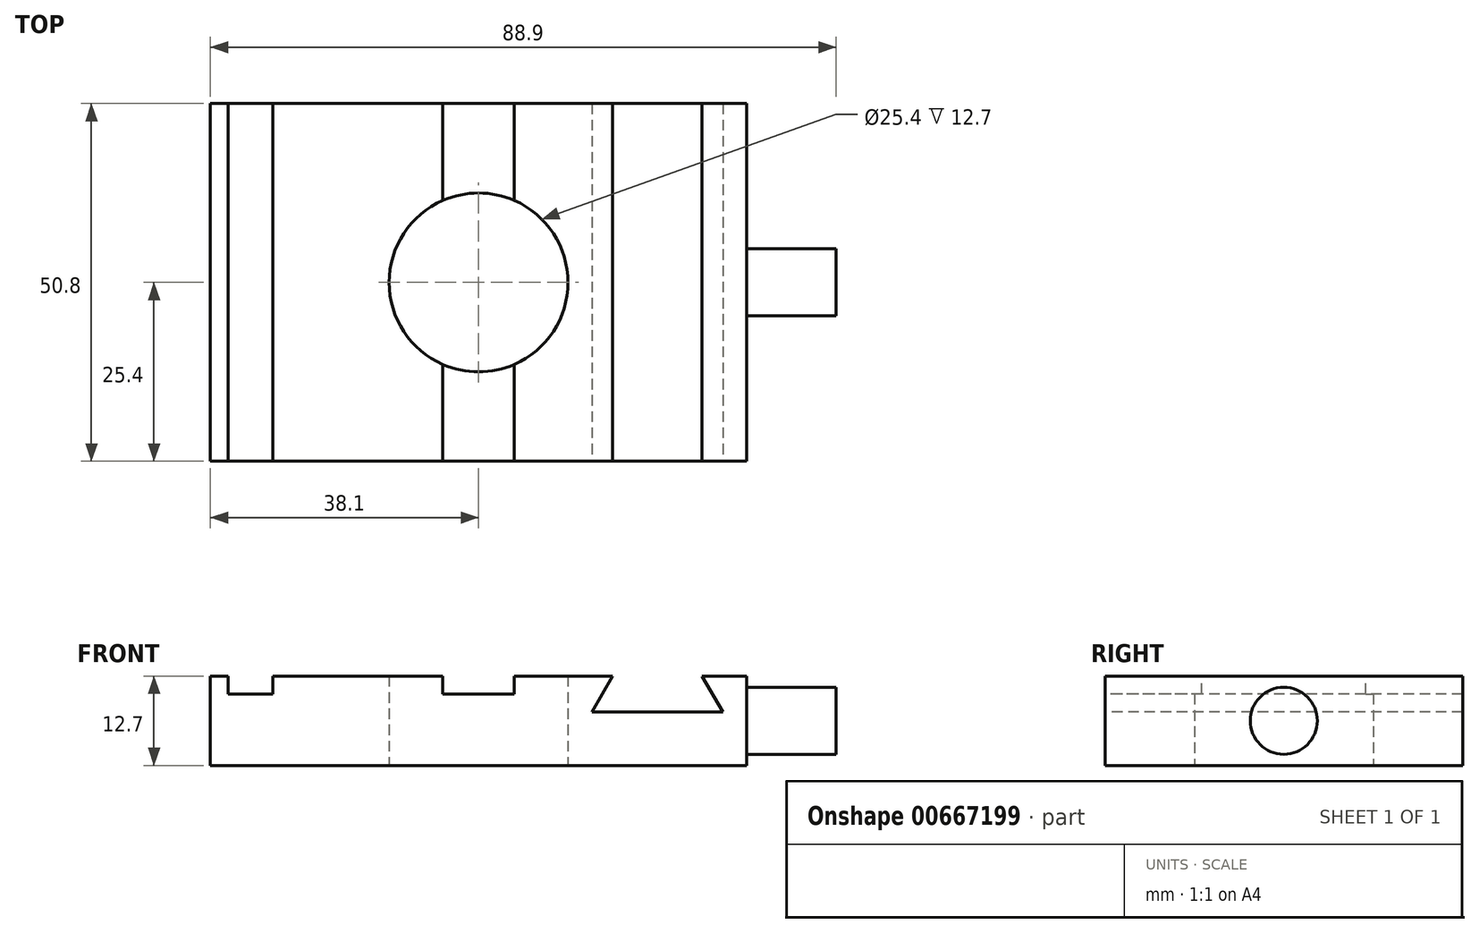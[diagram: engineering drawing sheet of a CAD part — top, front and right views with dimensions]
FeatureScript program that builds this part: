
annotation { "Feature Type Name" : "Feature", "Feature Type Description" : "" }
export const myFeature = defineFeature(function(context is Context, id is Id, definition is map)
    precondition{}
    {
        {
            var Q0;
            Q0=qCreatedBy(makeId("Top.planeOp"),FACE);
            var sketch = newSketch(context, id + "F0", { "sketchPlane" : qUnion([Q0])});
            skLineSegment(sketch, "E0.bottom", {"start": v(38.1, 25.4) * mm, "end": v(-38.1, 25.4) * mm});
            skLineSegment(sketch, "E0.top", {"start": v(38.1, -25.4) * mm, "end": v(-38.1, -25.4) * mm});
            skLineSegment(sketch, "E0.left", {"start": v(38.1, 25.4) * mm, "end": v(38.1, -25.4) * mm});
            skLineSegment(sketch, "E0.right", {"start": v(-38.1, 25.4) * mm, "end": v(-38.1, -25.4) * mm});
            skPoint(sketch, "E0.middle", {"position": v(0, 0) * mm});
            skCircle(sketch, "E1", {"center": v(0, 0) * mm, "radius": 12.7 * mm});
            skSolve(sketch);
        }
        {
            var Q0;
            Q0=makeQuery(id+"F0.imprint","IMPRINT",FACE,{"disambiguationData":[TD([[makeQuery(id+"F0.imprint","IMPRINT",EDGE,{"derivedFrom":sQuery(id+"F0.wireOp",EDGE,"E0.bottom")}),1.0]])]});
            extrude(context, id + "F1", {"entities" : qUnion([Q0]), "depth" : 12.7 * mm, "offsetDistance" : 25.4 * mm});
        }
        {
            var Q0;
            Q0=makeQuery(id+"F1.opExtrude","CAP_FACE",FACE,{"disambiguationData":[OSD([sQuery(id+"F0.wireOp",EDGE,"E0.bottom"),sQuery(id+"F0.wireOp",EDGE,"E0.top"),sQuery(id+"F0.wireOp",EDGE,"E0.left"),sQuery(id+"F0.wireOp",EDGE,"E0.right"),sQuery(id+"F0.wireOp",EDGE,"E1")])],"isStart":false});
            var sketch = newSketch(context, id + "F2", { "sketchPlane" : qUnion([Q0])});
            skLineSegment(sketch, "E2.bottom", {"start": v(-35.56, 25.4) * mm, "end": v(-29.21, 25.4) * mm});
            skLineSegment(sketch, "E2.top", {"start": v(-35.56, -25.4) * mm, "end": v(-29.21, -25.4) * mm});
            skLineSegment(sketch, "E2.left", {"start": v(-35.56, 25.4) * mm, "end": v(-35.56, -25.4) * mm});
            skLineSegment(sketch, "E2.right", {"start": v(-29.21, 25.4) * mm, "end": v(-29.21, -25.4) * mm});
            skLineSegment(sketch, "E3", {"start": v(-26.39, -25.4) * mm, "end": v(-8.27, -25.4) * mm});
            skPoint(sketch, "E4", {"position": v(0, 0) * mm});
            skLineSegment(sketch, "E5", {"start": v(-5.08, 25.4) * mm, "end": v(-5.08, -25.4) * mm});
            skLineSegment(sketch, "E6", {"start": v(-5.08, -25.4) * mm, "end": v(5.08, -25.4) * mm});
            skLineSegment(sketch, "E7", {"start": v(5.08, -25.4) * mm, "end": v(5.08, 25.4) * mm});
            skLineSegment(sketch, "E8", {"start": v(5.08, 25.4) * mm, "end": v(-5.08, 25.4) * mm});
            skLineSegment(sketch, "E9", {"start": v(0, 25.4) * mm, "end": v(0, -25.4) * mm, "construction": true});
            skSolve(sketch);
        }
        {
            var Q0;
            Q0=makeQuery(id+"F2.imprint","IMPRINT",FACE,{"disambiguationData":[TD([[makeQuery(id+"F2.imprint","IMPRINT",EDGE,{"derivedFrom":sQuery(id+"F2.wireOp",EDGE,"E2.bottom")}),1.0]])]});
            var Q1;
            {var subQ0=sQuery(id+"F2.wireOp",EDGE,"E6");Q1=makeQuery(id+"F2.imprint","IMPRINT",FACE,{"disambiguationData":[TD([[makeQuery(id+"F2.imprint","IMPRINT",EDGE,{"derivedFrom":subQ0}),-1.0]])]});}
            var Q2;
            {var subQ0=sQuery(id+"F2.wireOp",EDGE,"E8");Q2=makeQuery(id+"F2.imprint","IMPRINT",FACE,{"disambiguationData":[TD([[makeQuery(id+"F2.imprint","IMPRINT",EDGE,{"derivedFrom":subQ0}),1.0]])]});}
            extrude(context, id + "F3", {"entities" : qUnion([Q0, Q1, Q2]), "operationType" : NewBodyOperationType.REMOVE, "oppositeDirection" : true, "depth" : 2.54 * mm, "offsetDistance" : 25.4 * mm});
        }
        {
            var Q0;
            Q0=makeQuery(id+"F1.opExtrude","SWEPT_FACE",FACE,{"disambiguationData":[OSD([sQuery(id+"F0.wireOp",EDGE,"E0.top")])]});
            var sketch = newSketch(context, id + "F4", { "sketchPlane" : qUnion([Q0])});
            skLineSegment(sketch, "E10", {"start": v(19.05, 12.7) * mm, "end": v(16.12, 7.62) * mm});
            skLineSegment(sketch, "E11", {"start": v(16.12, 7.62) * mm, "end": v(34.68, 7.62) * mm});
            skLineSegment(sketch, "E12", {"start": v(34.68, 7.62) * mm, "end": v(31.75, 12.7) * mm});
            skLineSegment(sketch, "E13", {"start": v(31.75, 12.7) * mm, "end": v(19.05, 12.7) * mm});
            skLineSegment(sketch, "E14", {"start": v(25.4, 7.62) * mm, "end": v(25.4, 12.7) * mm, "construction": true});
            skSolve(sketch);
        }
        {
            var Q0;
            Q0=makeQuery(id+"F4.imprint","IMPRINT",FACE,{"disambiguationData":[TD([[makeQuery(id+"F4.imprint","IMPRINT",EDGE,{"derivedFrom":sQuery(id+"F4.wireOp",EDGE,"E10")}),1.0]])]});
            extrude(context, id + "F5", {"entities" : qUnion([Q0]), "operationType" : NewBodyOperationType.REMOVE, "endBound" : BoundingType.THROUGH_ALL, "oppositeDirection" : true, "depth" : 25.4 * mm, "offsetDistance" : 25.4 * mm});
        }
        {
            var Q0;
            Q0=makeQuery(id+"F1.opExtrude","SWEPT_FACE",FACE,{"disambiguationData":[OSD([sQuery(id+"F0.wireOp",EDGE,"E0.left")])]});
            var sketch = newSketch(context, id + "F6", { "sketchPlane" : qUnion([Q0])});
            skCircle(sketch, "E15", {"center": v(0, 6.35) * mm, "radius": 4.76 * mm});
            skPoint(sketch, "E15.centerSnap0", {"position": v(-25.4, 6.35) * mm});
            skPoint(sketch, "E15.centerSnap1", {"position": v(0, 12.7) * mm});
            skSolve(sketch);
        }
        {
            var Q0;
            Q0=makeQuery(id+"F6.imprint","IMPRINT",FACE,{"disambiguationData":[TD([[makeQuery(id+"F6.imprint","IMPRINT",EDGE,{"derivedFrom":sQuery(id+"F6.wireOp",EDGE,"E15")}),1.0]])]});
            extrude(context, id + "F7", {"entities" : qUnion([Q0]), "operationType" : NewBodyOperationType.ADD, "depth" : 12.7 * mm, "offsetDistance" : 25.4 * mm});
        }
    });
